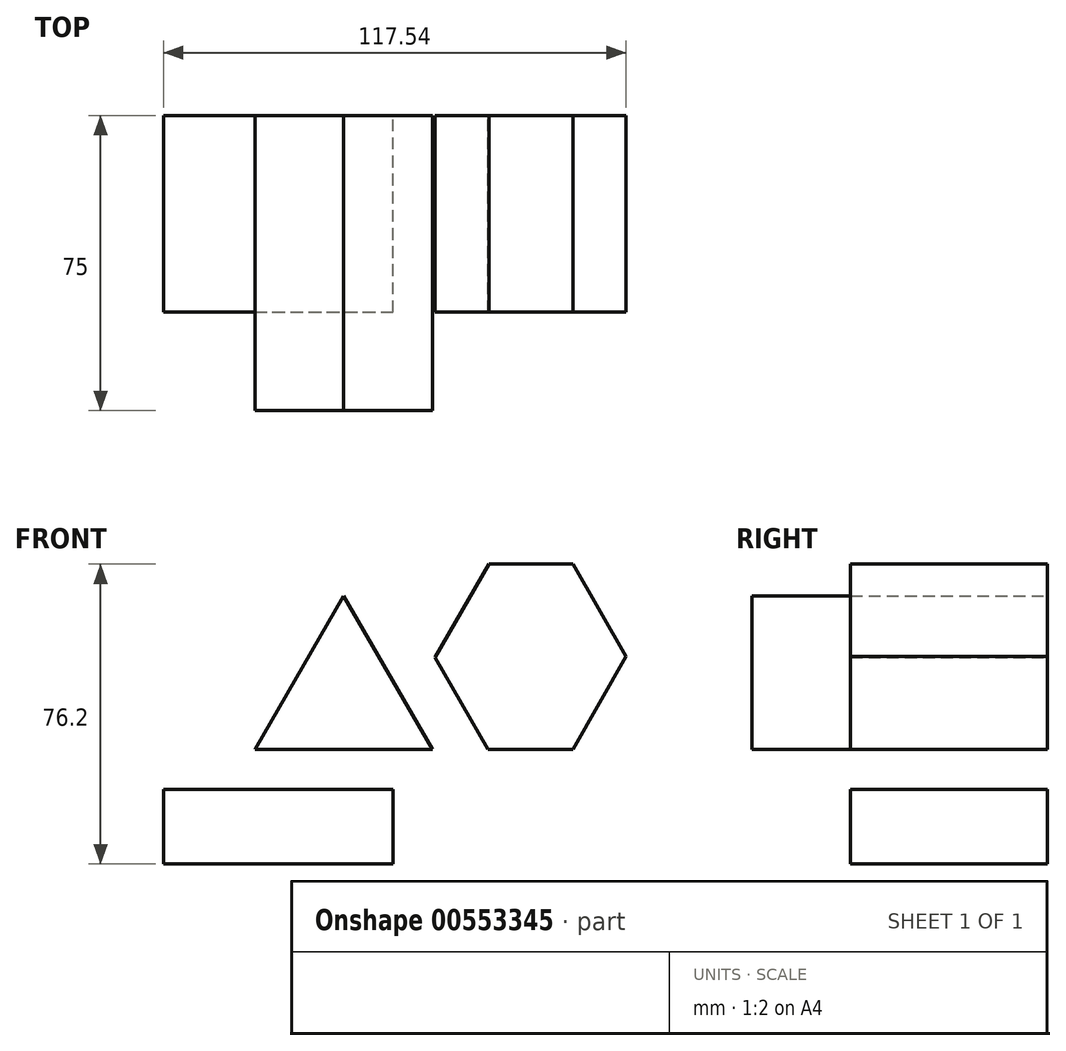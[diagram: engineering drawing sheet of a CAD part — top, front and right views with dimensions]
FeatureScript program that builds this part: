
annotation { "Feature Type Name" : "Feature", "Feature Type Description" : "" }
export const myFeature = defineFeature(function(context is Context, id is Id, definition is map)
    precondition{}
    {
        {
            var Q0;
            Q0=qCreatedBy(makeId("Front.planeOp"),FACE);
            var sketch = newSketch(context, id + "F0", { "sketchPlane" : qUnion([Q0])});
            skLineSegment(sketch, "E0", {"start": v(0, 0) * mm, "end": v(-22.5, 38.97) * mm});
            skLineSegment(sketch, "E1", {"start": v(-22.5, 38.97) * mm, "end": v(-45, 0) * mm});
            skLineSegment(sketch, "E2", {"start": v(-45, 0) * mm, "end": v(0, 0) * mm});
            skSolve(sketch);
        }
        {
            var Q0;
            Q0=makeQuery(id+"F0.imprint","IMPRINT",FACE,{"disambiguationData":[TD([[makeQuery(id+"F0.imprint","IMPRINT",EDGE,{"derivedFrom":sQuery(id+"F0.wireOp",EDGE,"E0")}),1.0]])]});
            extrude(context, id + "F1", {"entities" : qUnion([Q0]), "depth" : 25 * mm, "offsetDistance" : 25 * mm});
        }
        {
            var Q0;
            Q0=qCreatedBy(makeId("Front.planeOp"),FACE);
            var sketch = newSketch(context, id + "F2", { "sketchPlane" : qUnion([Q0])});
            skLineSegment(sketch, "E3", {"start": v(14.16, 0) * mm, "end": v(35.7, 0) * mm});
            skLineSegment(sketch, "E4", {"start": v(35.7, 0) * mm, "end": v(49.27, 23.51) * mm});
            skLineSegment(sketch, "E5", {"start": v(35.7, 47.02) * mm, "end": v(49.27, 23.51) * mm});
            skLineSegment(sketch, "E6", {"start": v(35.7, 47.02) * mm, "end": v(14.45, 47.02) * mm});
            skLineSegment(sketch, "E7", {"start": v(0.73, 23.27) * mm, "end": v(14.45, 47.02) * mm});
            skLineSegment(sketch, "E8", {"start": v(0.73, 23.27) * mm, "end": v(14.16, 0) * mm});
            skSolve(sketch);
        }
        {
            var Q0;
            Q0=makeQuery(id+"F2.imprint","IMPRINT",FACE,{"disambiguationData":[TD([[makeQuery(id+"F2.imprint","IMPRINT",EDGE,{"derivedFrom":sQuery(id+"F2.wireOp",EDGE,"E3")}),1.0]])]});
            extrude(context, id + "F3", {"entities" : qUnion([Q0]), "depth" : 50 * mm, "offsetDistance" : 25 * mm});
        }
        {
            var Q0;
            Q0=makeQuery(id+"F1.opExtrude","CAP_FACE",FACE,{"disambiguationData":[OSD([sQuery(id+"F0.wireOp",EDGE,"E0"),sQuery(id+"F0.wireOp",EDGE,"E1"),sQuery(id+"F0.wireOp",EDGE,"E2")])],"isStart":false});
            extrude(context, id + "F4", {"entities" : qUnion([Q0]), "operationType" : NewBodyOperationType.ADD, "depth" : 50 * mm, "offsetDistance" : 25 * mm});
        }
        {
            var Q0;
            Q0=qCreatedBy(makeId("Front.planeOp"),FACE);
            var sketch = newSketch(context, id + "F5", { "sketchPlane" : qUnion([Q0])});
            skLineSegment(sketch, "E9.bottom", {"start": v(-68.27, -10.2) * mm, "end": v(-9.91, -10.2) * mm});
            skLineSegment(sketch, "E9.top", {"start": v(-68.27, -29.18) * mm, "end": v(-9.91, -29.18) * mm});
            skLineSegment(sketch, "E9.left", {"start": v(-68.27, -10.2) * mm, "end": v(-68.27, -29.18) * mm});
            skLineSegment(sketch, "E9.right", {"start": v(-9.91, -10.2) * mm, "end": v(-9.91, -29.18) * mm});
            skSolve(sketch);
        }
        {
            var Q0;
            Q0=makeQuery(id+"F5.imprint","IMPRINT",FACE,{"disambiguationData":[TD([[makeQuery(id+"F5.imprint","IMPRINT",EDGE,{"derivedFrom":sQuery(id+"F5.wireOp",EDGE,"E9.bottom")}),-1.0]])]});
            extrude(context, id + "F6", {"entities" : qUnion([Q0]), "depth" : 50 * mm, "offsetDistance" : 25 * mm});
        }
    });
